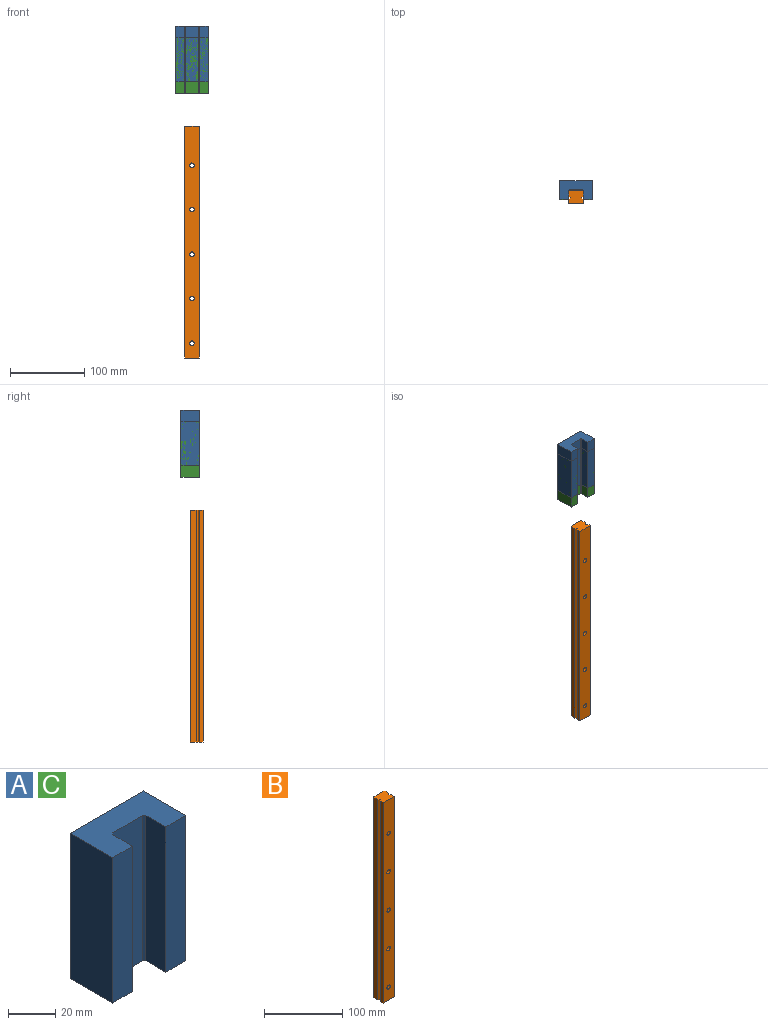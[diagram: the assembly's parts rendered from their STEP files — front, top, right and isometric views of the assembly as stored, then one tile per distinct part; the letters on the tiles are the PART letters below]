
ASSEMBLY  parts=3 mates=4
PART A: 20 faces, bbox 44x25.4x75.5 mm
  f0: plane 75.5x44mm, normal (0,1,0), area 3243.5mm2, adj f1,f9,f10,f11,f12,f14,f16,f18
  f1: plane 75.5x25.4mm, normal (-1,0,0), area 1917.7mm2, adj f0,f2,f10,f11
  f2: plane 75.5x12mm, normal (0,-1,0), area 906mm2, adj f1,f3,f10,f11
  f3: plane 75.5x11.9mm, normal (1,0,0), area 898.4mm2, adj f2,f4,f10,f11
  f4: plane 75.5x1mm, normal (0.71,-0.71,0), area 106.8mm2, adj f3,f5,f10,f11
  f5: plane 75.5x18mm, normal (0,-1,0), area 1359mm2, adj f4,f6,f10,f11
  f6: plane 75.5x1mm, normal (-0.71,-0.71,0), area 106.8mm2, adj f5,f7,f10,f11
  f7: plane 75.5x11.9mm, normal (-1,0,0), area 898.4mm2, adj f6,f8,f10,f11
  f8: plane 75.5x12mm, normal (0,-1,0), area 906mm2, adj f7,f9,f10,f11
  f9: plane 75.5x25.4mm, normal (1,0,0), area 1917.7mm2, adj f0,f8,f10,f11
  f10: plane 44x25.4mm, normal (0,0,1), area 860.6mm2, adj f0,f1,f2,f3,f4,f5,f6,f7
  f11: plane 44x25.4mm, normal (0,0,-1), area 860.6mm2, adj f0,f1,f2,f3,f4,f5,f6,f7
  f12: cylinder r=2.5mm len=5mm, axis (0,1,0), area 78.5mm2, adj f0,f13
  f13: plane 5x5mm, normal (0,1,0), area 19.6mm2, adj f12
  f14: cylinder r=2.5mm len=5mm, axis (0,1,0), area 78.5mm2, adj f0,f15
  f15: plane 5x5mm, normal (0,1,0), area 19.6mm2, adj f14
  f16: cylinder r=2.5mm len=5mm, axis (0,1,0), area 78.5mm2, adj f0,f17
  f17: plane 5x5mm, normal (0,1,0), area 19.6mm2, adj f16
  f18: cylinder r=2.5mm len=5mm, axis (0,1,0), area 78.5mm2, adj f0,f19
  f19: plane 5x5mm, normal (0,1,0), area 19.6mm2, adj f18
PART B: 29 faces, bbox 20x17.5x312.7 mm
  f0: plane 312.7x2.5mm, normal (0.72,-0.69,0), area 1084.4mm2, adj f1,f11,f12,f13
  f1: plane 312.7x6.9mm, normal (1,0,0), area 2157.6mm2, adj f0,f2,f12,f13
  f2: plane 312.7x1mm, normal (0.71,0.71,0), area 442.2mm2, adj f1,f3,f12,f13
  f3: plane 312.7x18mm, normal (0,1,0), area 5274.2mm2, adj f2,f4,f12,f13,f14,f17,f20,f23
  f4: plane 312.7x1mm, normal (-0.71,0.71,0), area 442.2mm2, adj f3,f5,f12,f13
  f5: plane 312.7x6.9mm, normal (-1,0,0), area 2157.6mm2, adj f4,f6,f12,f13
  f6: plane 312.7x2.5mm, normal (-0.72,-0.69,0), area 1084.4mm2, adj f5,f7,f12,f13
  f7: plane 312.7x2.5mm, normal (-0.72,0.69,0), area 1084.4mm2, adj f6,f8,f12,f13
  f8: plane 312.7x4.6mm, normal (-1,0,0), area 1438.4mm2, adj f7,f9,f12,f13
  f9: plane 312.7x20mm, normal (0,-1,0), area 6112.6mm2, adj f8,f10,f12,f13,f16,f19,f22,f25
  f10: plane 312.7x4.6mm, normal (1,0,0), area 1438.4mm2, adj f9,f11,f12,f13
  f11: plane 312.7x2.5mm, normal (0.72,0.69,0), area 1084.4mm2, adj f0,f10,f12,f13
  f12: plane 20x17.5mm, normal (0,0,1), area 337mm2, adj f0,f1,f2,f3,f4,f5,f6,f7
  f13: plane 20x17.5mm, normal (0,0,-1), area 337mm2, adj f0,f1,f2,f3,f4,f5,f6,f7
  f14: cylinder r=4.75mm len=9.5mm, axis (0,1,0), area 253.7mm2, adj f3,f15
  f15: plane 9.5x9.5mm, normal (0,1,0), area 42.6mm2, adj f14,f16
  f16: cylinder r=3mm len=9mm, axis (0,1,0), area 169.6mm2, adj f9,f15
  f17: cylinder r=4.75mm len=9.5mm, axis (0,1,0), area 253.7mm2, adj f3,f18
  f18: plane 9.5x9.5mm, normal (0,1,0), area 42.6mm2, adj f17,f19
  f19: cylinder r=3mm len=9mm, axis (0,1,0), area 169.6mm2, adj f9,f18
  f20: cylinder r=4.75mm len=9.5mm, axis (0,1,0), area 253.7mm2, adj f3,f21
  f21: plane 9.5x9.5mm, normal (0,1,0), area 42.6mm2, adj f20,f22
  f22: cylinder r=3mm len=9mm, axis (0,1,0), area 169.6mm2, adj f9,f21
  f23: cylinder r=4.75mm len=9.5mm, axis (0,1,0), area 253.7mm2, adj f3,f24
  f24: plane 9.5x9.5mm, normal (0,1,0), area 42.6mm2, adj f23,f25
  f25: cylinder r=3mm len=9mm, axis (0,1,0), area 169.6mm2, adj f9,f24
  f26: cylinder r=4.75mm len=9.5mm, axis (0,1,0), area 253.7mm2, adj f3,f27
  f27: plane 9.5x9.5mm, normal (0,1,0), area 42.6mm2, adj f26,f28
  f28: cylinder r=3mm len=9mm, axis (0,1,0), area 169.6mm2, adj f9,f27
PART C: same geometry as A
PLACE A t=(-99.15,147.51,372.25)mm
PLACE B at identity
PLACE C t=(-99.15,147.51,356.95)mm
MATE planar C.f5 <-> B.f3  axis (0,-1,0) through (-7.08,30.61,394.7)mm
MATE planar C.f3 <-> B.f5  axis (1,0,0) through (-17.08,23.66,394.7)mm
MATE planar A.f5 <-> B.f3  axis (0,-1,0) through (-7.08,30.61,410)mm
MATE planar A.f3 <-> B.f5  axis (1,0,0) through (-17.08,23.66,410)mm
